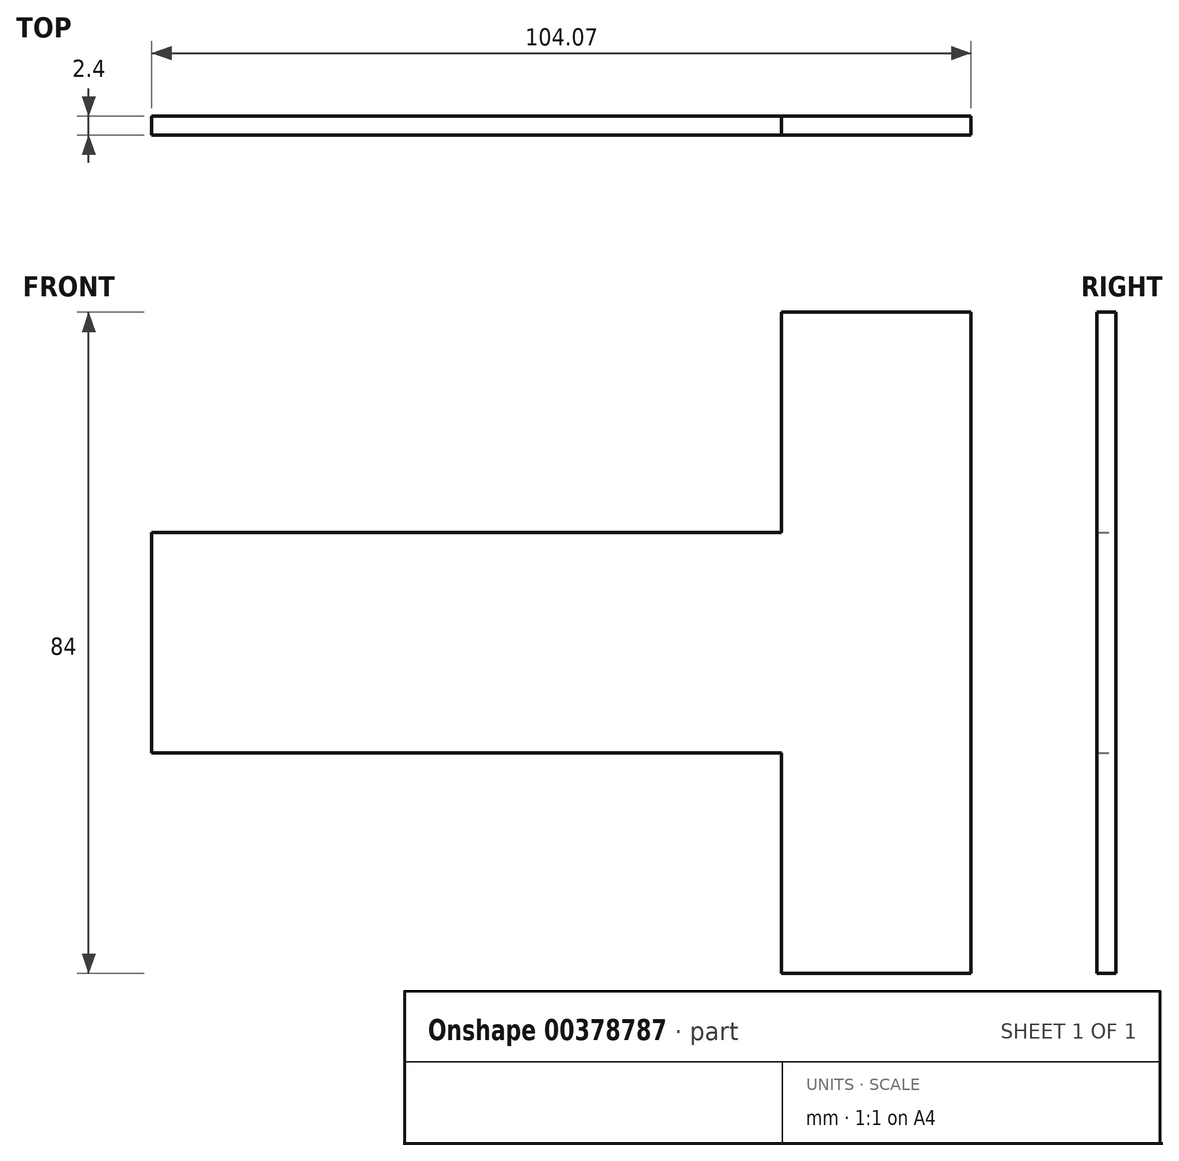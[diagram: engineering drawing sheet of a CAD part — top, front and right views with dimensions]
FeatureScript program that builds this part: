
annotation { "Feature Type Name" : "Feature", "Feature Type Description" : "" }
export const myFeature = defineFeature(function(context is Context, id is Id, definition is map)
    precondition{}
    {
        {
            var Q0;
            Q0=qCreatedBy(makeId("Front.planeOp"),FACE);
            var sketch = newSketch(context, id + "F0", { "sketchPlane" : qUnion([Q0])});
            skLineSegment(sketch, "E0.bottom", {"start": v(0, 0) * mm, "end": v(159.2, 0) * mm});
            skLineSegment(sketch, "E0.top", {"start": v(0, -28) * mm, "end": v(159.2, -28) * mm});
            skLineSegment(sketch, "E0.left", {"start": v(0, 0) * mm, "end": v(0, -28) * mm});
            skLineSegment(sketch, "E0.right", {"start": v(159.2, 0) * mm, "end": v(159.2, -28) * mm});
            skLineSegment(sketch, "E1", {"start": v(52, 0) * mm, "end": v(80, -28) * mm});
            skLineSegment(sketch, "E2", {"start": v(159.2, -28) * mm, "end": v(131.2, 0) * mm});
            skLineSegment(sketch, "E3", {"start": v(131.2, 0) * mm, "end": v(111.4, -19.8) * mm});
            skLineSegment(sketch, "E4", {"start": v(111.4, -19.8) * mm, "end": v(119.6, -28) * mm});
            skLineSegment(sketch, "E5", {"start": v(80, -28) * mm, "end": v(80, -56) * mm});
            skLineSegment(sketch, "E6", {"start": v(80, -56) * mm, "end": v(104.07, -56) * mm});
            skLineSegment(sketch, "E7", {"start": v(104.07, -56) * mm, "end": v(104.07, 28) * mm});
            skLineSegment(sketch, "E8", {"start": v(104.07, 28) * mm, "end": v(80, 28) * mm});
            skLineSegment(sketch, "E9", {"start": v(80, 28) * mm, "end": v(80, 0) * mm});
            skSolve(sketch);
        }
        {
            var Q0;
            {var subQ4=sQuery(id+"F0.wireOp",EDGE,"E8");Q0=makeQuery(id+"F0.imprint","IMPRINT",FACE,{"disambiguationData":[TD([[makeQuery(id+"F0.imprint","IMPRINT",EDGE,{"derivedFrom":subQ4}),1.0]])]});}
            var Q1;
            {var subQ4=sQuery(id+"F0.wireOp",EDGE,"E1");Q1=makeQuery(id+"F0.imprint","IMPRINT",FACE,{"disambiguationData":[TD([[makeQuery(id+"F0.imprint","IMPRINT",EDGE,{"derivedFrom":subQ4}),1.0]])]});}
            var Q2;
            {var subQ0=sQuery(id+"F0.wireOp",EDGE,"E5");Q2=makeQuery(id+"F0.imprint","IMPRINT",FACE,{"disambiguationData":[TD([[makeQuery(id+"F0.imprint","IMPRINT",EDGE,{"derivedFrom":subQ0}),1.0]])]});}
            var Q3;
            {var subQ0=sQuery(id+"F0.wireOp",EDGE,"E0.left");Q3=makeQuery(id+"F0.imprint","IMPRINT",FACE,{"disambiguationData":[TD([[makeQuery(id+"F0.imprint","IMPRINT",EDGE,{"derivedFrom":subQ0}),1.0]])]});}
            extrude(context, id + "F1", {"entities" : qUnion([Q0, Q1, Q2, Q3]), "depth" : 2.4 * mm});
        }
    });
